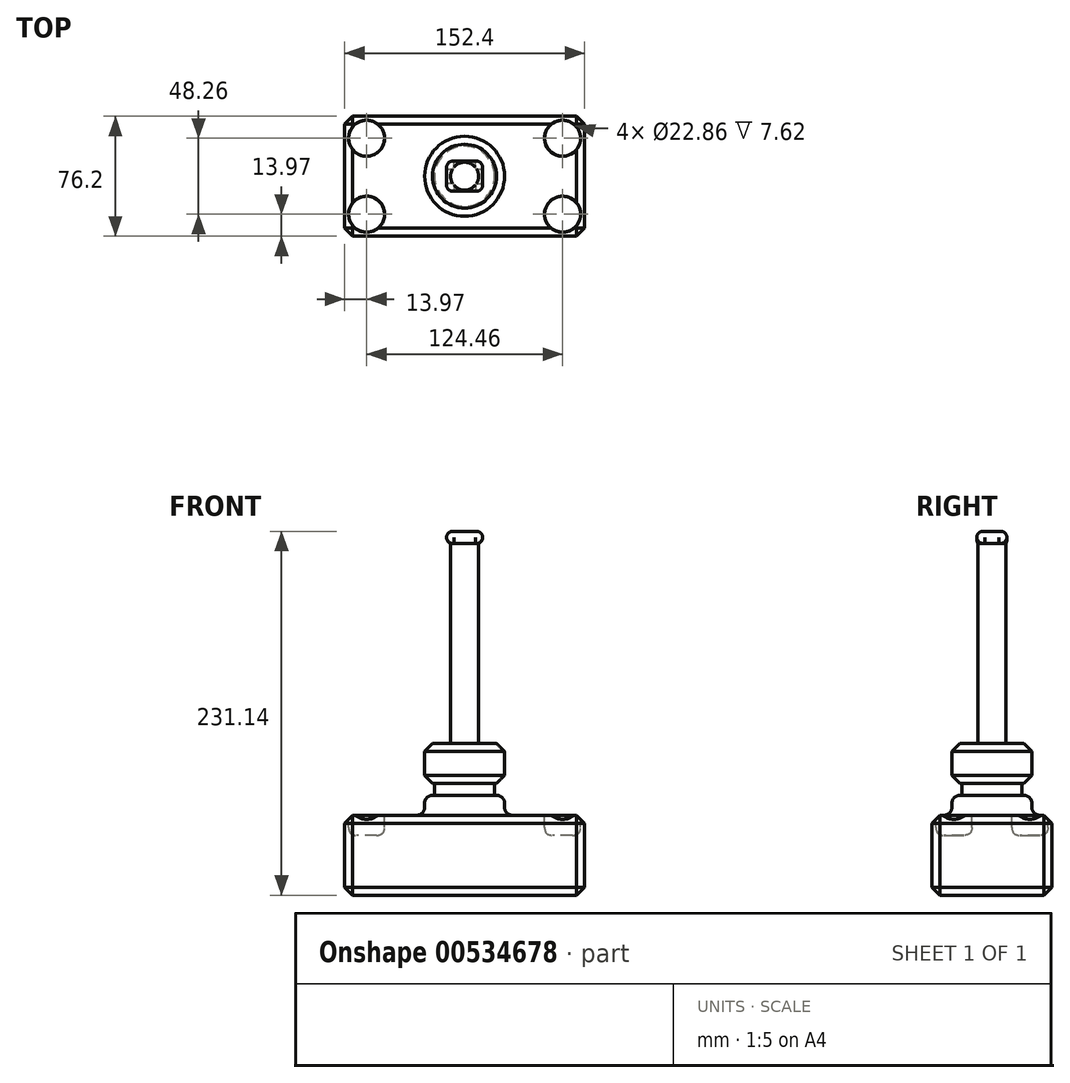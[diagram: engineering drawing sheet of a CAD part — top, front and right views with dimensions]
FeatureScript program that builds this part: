
annotation { "Feature Type Name" : "Feature", "Feature Type Description" : "" }
export const myFeature = defineFeature(function(context is Context, id is Id, definition is map)
    precondition{}
    {
        {
            var Q0;
            Q0=qCreatedBy(makeId("Top.planeOp"),FACE);
            var sketch = newSketch(context, id + "F0", { "sketchPlane" : qUnion([Q0])});
            skLineSegment(sketch, "E0.bottom", {"start": v(76.2, -38.1) * mm, "end": v(-76.2, -38.1) * mm});
            skLineSegment(sketch, "E0.top", {"start": v(76.2, 38.1) * mm, "end": v(-76.2, 38.1) * mm});
            skLineSegment(sketch, "E0.left", {"start": v(76.2, -38.1) * mm, "end": v(76.2, 38.1) * mm});
            skLineSegment(sketch, "E0.right", {"start": v(-76.2, -38.1) * mm, "end": v(-76.2, 38.1) * mm});
            skPoint(sketch, "E0.middle", {"position": v(0, 0) * mm});
            skSolve(sketch);
        }
        {
            var Q0;
            Q0 = qSketchRegion(id + "F0", true);
            extrude(context, id + "F1", {"entities" : qUnion([Q0]), "depth" : 50.8 * mm, "offsetDistance" : 25.4 * mm});
        }
        {
            var Q0;
            Q0=makeQuery(id+"F1.opExtrude","CAP_FACE",FACE,{"disambiguationData":[OSD([sQuery(id+"F0.wireOp",EDGE,"E0.bottom"),sQuery(id+"F0.wireOp",EDGE,"E0.top"),sQuery(id+"F0.wireOp",EDGE,"E0.left"),sQuery(id+"F0.wireOp",EDGE,"E0.right")])],"isStart":false});
            var sketch = newSketch(context, id + "F2", { "sketchPlane" : qUnion([Q0])});
            skCircle(sketch, "E1", {"center": v(0, 0) * mm, "radius": 25.4 * mm});
            skSolve(sketch);
        }
        {
            var Q0;
            Q0 = qSketchRegion(id + "F2", true);
            extrude(context, id + "F3", {"entities" : qUnion([Q0]), "operationType" : NewBodyOperationType.ADD, "depth" : 12.7 * mm, "offsetDistance" : 25.4 * mm});
        }
        {
            var Q0;
            Q0=makeQuery(id+"F3.opExtrude","CAP_FACE",FACE,{"disambiguationData":[OSD([sQuery(id+"F2.wireOp",EDGE,"E1")])],"isStart":false});
            var sketch = newSketch(context, id + "F4", { "sketchPlane" : qUnion([Q0])});
            skCircle(sketch, "E2", {"center": v(0, 0) * mm, "radius": 19.05 * mm});
            skSolve(sketch);
        }
        {
            var Q0;
            Q0 = qSketchRegion(id + "F4", true);
            extrude(context, id + "F5", {"entities" : qUnion([Q0]), "operationType" : NewBodyOperationType.ADD, "depth" : 7.62 * mm, "offsetDistance" : 25.4 * mm});
        }
        {
            var Q0;
            Q0=makeQuery(id+"F5.opExtrude","CAP_FACE",FACE,{"disambiguationData":[OSD([sQuery(id+"F4.wireOp",EDGE,"E2")])],"isStart":false});
            var sketch = newSketch(context, id + "F6", { "sketchPlane" : qUnion([Q0])});
            skCircle(sketch, "E3", {"center": v(0, 0) * mm, "radius": 25.4 * mm});
            skSolve(sketch);
        }
        {
            var Q0;
            Q0 = qSketchRegion(id + "F6", true);
            extrude(context, id + "F7", {"entities" : qUnion([Q0]), "operationType" : NewBodyOperationType.ADD, "depth" : 25.4 * mm, "offsetDistance" : 25.4 * mm});
        }
        {
            var Q0;
            Q0=makeQuery(id+"F1.opExtrude","CAP_FACE",FACE,{"disambiguationData":[OSD([sQuery(id+"F0.wireOp",EDGE,"E0.bottom"),sQuery(id+"F0.wireOp",EDGE,"E0.top"),sQuery(id+"F0.wireOp",EDGE,"E0.left"),sQuery(id+"F0.wireOp",EDGE,"E0.right")])],"isStart":false});
            var sketch = newSketch(context, id + "F8", { "sketchPlane" : qUnion([Q0])});
            skCircle(sketch, "E4", {"center": v(-62.23, 24.13) * mm, "radius": 11.43 * mm});
            skCircle(sketch, "E5", {"center": v(62.23, 24.13) * mm, "radius": 11.43 * mm});
            skCircle(sketch, "E6", {"center": v(62.23, -24.13) * mm, "radius": 11.43 * mm});
            skCircle(sketch, "E7", {"center": v(-62.23, -24.13) * mm, "radius": 11.43 * mm});
            skSolve(sketch);
        }
        {
            var Q0;
            Q0 = qSketchRegion(id + "F8", true);
            extrude(context, id + "F9", {"entities" : qUnion([Q0]), "operationType" : NewBodyOperationType.REMOVE, "oppositeDirection" : true, "depth" : 12.7 * mm, "offsetDistance" : 25.4 * mm});
        }
        {
            var Q0;
            Q0=makeQuery(id+"F1.opExtrude","SWEPT_FACE",FACE,{"disambiguationData":[OSD([sQuery(id+"F0.wireOp",EDGE,"E0.right")])]});
            var Q1;
            Q1=makeQuery(id+"F1.opExtrude","SWEPT_FACE",FACE,{"disambiguationData":[OSD([sQuery(id+"F0.wireOp",EDGE,"E0.top")])]});
            var Q2;
            Q2=makeQuery(id+"F1.opExtrude","CAP_EDGE",EDGE,{"disambiguationData":[OSD([sQuery(id+"F0.wireOp",EDGE,"E0.left")])],"isStart":false});
            var Q3;
            Q3=makeQuery(id+"F1.opExtrude","SWEPT_FACE",FACE,{"disambiguationData":[OSD([sQuery(id+"F0.wireOp",EDGE,"E0.bottom")])]});
            var Q4;
            Q4=makeQuery(id+"F1.opExtrude","CAP_FACE",FACE,{"disambiguationData":[OSD([sQuery(id+"F0.wireOp",EDGE,"E0.bottom"),sQuery(id+"F0.wireOp",EDGE,"E0.top"),sQuery(id+"F0.wireOp",EDGE,"E0.left"),sQuery(id+"F0.wireOp",EDGE,"E0.right")])],"isStart":true});
            var Q5;
            Q5=makeQuery(id+"F1.opExtrude","SWEPT_FACE",FACE,{"disambiguationData":[OSD([sQuery(id+"F0.wireOp",EDGE,"E0.left")])]});
            chamfer(context, id + "F10", {"entities" : qUnion([Q0, Q1, Q2, Q3, Q4, Q5]), "width" : 5.08 * mm, "tangentPropagation" : true});
        }
        {
            var Q0;
            Q0=makeQuery(id+"F7.opExtrude","CAP_FACE",FACE,{"disambiguationData":[OSD([sQuery(id+"F6.wireOp",EDGE,"E3")])],"isStart":false});
            var sketch = newSketch(context, id + "F11", { "sketchPlane" : qUnion([Q0])});
            skCircle(sketch, "E8", {"center": v(0, 0) * mm, "radius": 8.9 * mm});
            skSolve(sketch);
        }
        {
            var Q0;
            Q0 = qSketchRegion(id + "F11", true);
            extrude(context, id + "F12", {"entities" : qUnion([Q0]), "operationType" : NewBodyOperationType.ADD, "depth" : 127 * mm, "offsetDistance" : 25.4 * mm});
        }
        {
            var Q0;
            Q0=makeQuery(id+"F12.opExtrude","CAP_FACE",FACE,{"disambiguationData":[OSD([sQuery(id+"F11.wireOp",EDGE,"E8")])],"isStart":false});
            var sketch = newSketch(context, id + "F13", { "sketchPlane" : qUnion([Q0])});
            skLineSegment(sketch, "E9.bottom", {"start": v(11.43, -9.53) * mm, "end": v(-11.43, -9.53) * mm});
            skLineSegment(sketch, "E9.top", {"start": v(11.43, 9.53) * mm, "end": v(-11.43, 9.52) * mm});
            skLineSegment(sketch, "E9.left", {"start": v(11.43, -9.53) * mm, "end": v(11.43, 9.53) * mm});
            skLineSegment(sketch, "E9.right", {"start": v(-11.43, -9.53) * mm, "end": v(-11.43, 9.52) * mm});
            skPoint(sketch, "E9.middle", {"position": v(0, 0) * mm});
            skSolve(sketch);
        }
        {
            var Q0;
            Q0 = qSketchRegion(id + "F13", true);
            extrude(context, id + "F14", {"entities" : qUnion([Q0]), "operationType" : NewBodyOperationType.ADD, "depth" : 7.62 * mm, "offsetDistance" : 25.4 * mm});
        }
        {
            var Q0;
            Q0=makeQuery(id+"F7.opExtrude","SWEPT_FACE",FACE,{"disambiguationData":[OSD([sQuery(id+"F6.wireOp",EDGE,"E3")])]});
            chamfer(context, id + "F15", {"entities" : qUnion([Q0]), "width" : 5.08 * mm, "tangentPropagation" : true});
        }
        {
            var Q0;
            Q0=makeQuery(id+"F3.opExtrude","SWEPT_FACE",FACE,{"disambiguationData":[OSD([sQuery(id+"F2.wireOp",EDGE,"E1")])]});
            fillet(context, id + "F16", {"entities" : qUnion([Q0]), "radius" : 5.08 * mm, "tangentPropagation" : true, "allowEdgeOverflow" : false});
        }
        {
            var Q0;
            Q0=makeQuery(id+"F9.boolean.opBoolean","COPY",FACE,{"derivedFrom":makeQuery(id+"F9.opExtrude","CAP_FACE",FACE,{"disambiguationData":[OSD([sQuery(id+"F8.wireOp",EDGE,"E5")])],"isStart":false})});
            var Q1;
            Q1=makeQuery(id+"F9.boolean.opBoolean","COPY",FACE,{"derivedFrom":makeQuery(id+"F9.opExtrude","CAP_FACE",FACE,{"disambiguationData":[OSD([sQuery(id+"F8.wireOp",EDGE,"E6")])],"isStart":false})});
            var Q2;
            Q2=makeQuery(id+"F9.boolean.opBoolean","COPY",FACE,{"derivedFrom":makeQuery(id+"F9.opExtrude","CAP_FACE",FACE,{"disambiguationData":[OSD([sQuery(id+"F8.wireOp",EDGE,"E7")])],"isStart":false})});
            var Q3;
            Q3=makeQuery(id+"F9.boolean.opBoolean","COPY",FACE,{"derivedFrom":makeQuery(id+"F9.opExtrude","CAP_FACE",FACE,{"disambiguationData":[OSD([sQuery(id+"F8.wireOp",EDGE,"E4")])],"isStart":false})});
            fillet(context, id + "F17", {"entities" : qUnion([Q0, Q1, Q2, Q3]), "radius" : 5.08 * mm, "tangentPropagation" : true, "rho" : 0.5, "crossSection" : FilletCrossSection.CONIC, "allowEdgeOverflow" : false});
        }
        {
            var Q0;
            Q0=makeQuery(id+"F14.opExtrude","CAP_EDGE",EDGE,{"disambiguationData":[OSD([sQuery(id+"F13.wireOp",EDGE,"E9.bottom")])],"isStart":true});
            var Q1;
            Q1=makeQuery(id+"F14.opExtrude","SWEPT_FACE",FACE,{"disambiguationData":[OSD([sQuery(id+"F13.wireOp",EDGE,"E9.top")])]});
            var Q2;
            Q2=makeQuery(id+"F14.opExtrude","CAP_EDGE",EDGE,{"disambiguationData":[OSD([sQuery(id+"F13.wireOp",EDGE,"E9.bottom")])],"isStart":false});
            var Q3;
            Q3=makeQuery(id+"F14.opExtrude","SWEPT_FACE",FACE,{"disambiguationData":[OSD([sQuery(id+"F13.wireOp",EDGE,"E9.left")])]});
            var Q4;
            Q4=makeQuery(id+"F14.opExtrude","CAP_FACE",FACE,{"disambiguationData":[OSD([sQuery(id+"F13.wireOp",EDGE,"E9.bottom"),sQuery(id+"F13.wireOp",EDGE,"E9.top"),sQuery(id+"F13.wireOp",EDGE,"E9.left"),sQuery(id+"F13.wireOp",EDGE,"E9.right")])],"isStart":false});
            var Q5;
            Q5=makeQuery(id+"F14.opExtrude","SWEPT_FACE",FACE,{"disambiguationData":[OSD([sQuery(id+"F13.wireOp",EDGE,"E9.bottom")])]});
            var Q6;
            Q6=makeQuery(id+"F14.opExtrude","CAP_EDGE",EDGE,{"disambiguationData":[OSD([sQuery(id+"F13.wireOp",EDGE,"E9.right")])],"isStart":true});
            fillet(context, id + "F18", {"entities" : qUnion([Q0, Q1, Q2, Q3, Q4, Q5, Q6]), "radius" : 3.8 * mm, "tangentPropagation" : true, "allowEdgeOverflow" : false});
        }
    });
